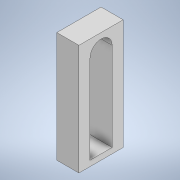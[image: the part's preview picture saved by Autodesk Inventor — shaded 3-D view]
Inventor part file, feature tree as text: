
AUTODESK INVENTOR PART (.ipt)
format: ipt  version: 2022 (Build 260153000, 153)  size: 109,056 bytes
history: native  units: mm
features: extrude x2, sketch x2, other x1
ambient origin geometry x8: Origin, YZ Plane, XZ Plane, XY Plane, X Axis, Y Axis, Z Axis, Center Point
bodies: Body1 (feature_tree)
feature tree (5):
  other  "솔리드1"
  extrude  "돌출1"  Depth=5.0mm
  extrude  "돌출2"  Depth=2.0mm
  sketch  "스케치1"
  sketch  "스케치3"
